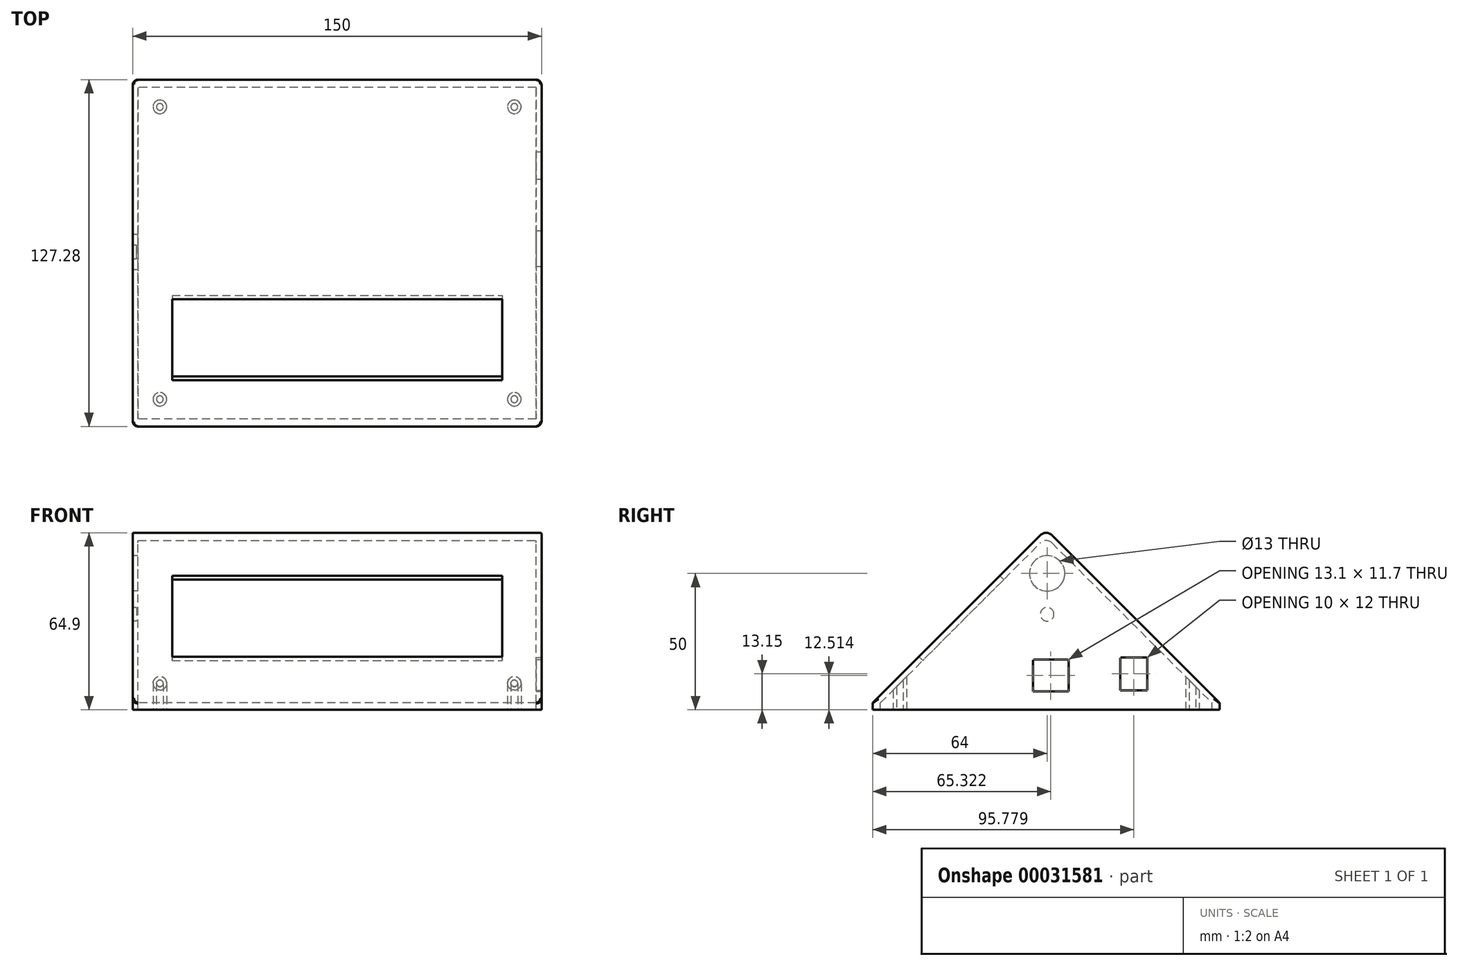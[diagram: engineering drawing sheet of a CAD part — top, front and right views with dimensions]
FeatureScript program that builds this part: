
annotation { "Feature Type Name" : "Feature", "Feature Type Description" : "" }
export const myFeature = defineFeature(function(context is Context, id is Id, definition is map)
    precondition{}
    {
        {
            var Q0;
            Q0=qCreatedBy(makeId("Right.planeOp"),FACE);
            var sketch = newSketch(context, id + "F0", { "sketchPlane" : qUnion([Q0])});
            skLineSegment(sketch, "E0", {"start": v(0, 0) * mm, "end": v(63.64, 63.64) * mm});
            skLineSegment(sketch, "E1", {"start": v(63.64, 63.64) * mm, "end": v(127.28, 0) * mm});
            skLineSegment(sketch, "E2", {"start": v(127.28, 0) * mm, "end": v(0, 0) * mm});
            skSolve(sketch);
        }
        {
            var Q0;
            Q0=qSketchRegion(id+"F0",true);
            extrude(context, id + "F1", {"entities" : qUnion([Q0]), "depth" : 150 * mm});
        }
        {
            var Q0;
            Q0=makeQuery(id+"F1.opExtrude","SWEPT_FACE",FACE,{"disambiguationData":[OSD([sQuery(id+"F0.wireOp",EDGE,"E2")])]});
            shell(context, id + "F2", {"entities" : qUnion([Q0]), "thickness" : 2 * mm});
        }
        {
            var Q0;
            Q0=makeQuery(id+"F1.opExtrude","SWEPT_FACE",FACE,{"disambiguationData":[OSD([sQuery(id+"F0.wireOp",EDGE,"E0")])]});
            cPlane(context, id + "F3", {"entities" : qUnion([Q0]), "cplaneType" : CPlaneType.OFFSET, "offset" : 0 * mm, "width" : 150 * mm, "height" : 150 * mm});
        }
        {
            var Q0;
            Q0=qCreatedBy(id+"F3.planeOp",FACE);
            var sketch = newSketch(context, id + "F4", { "sketchPlane" : qUnion([Q0])});
            skLineSegment(sketch, "E3.bottom", {"start": v(14.5, 66) * mm, "end": v(135.5, 66) * mm});
            skLineSegment(sketch, "E3.top", {"start": v(14.5, 24) * mm, "end": v(135.5, 24) * mm});
            skLineSegment(sketch, "E3.left", {"start": v(14.5, 66) * mm, "end": v(14.5, 24) * mm});
            skLineSegment(sketch, "E3.right", {"start": v(135.5, 66) * mm, "end": v(135.5, 24) * mm});
            skLineSegment(sketch, "E4", {"start": v(14.5, 45) * mm, "end": v(90.75, 45) * mm, "construction": true});
            skSolve(sketch);
        }
        {
            var Q0;
            Q0=qSketchRegion(id+"F4",true);
            extrude(context, id + "F5", {"entities" : qUnion([Q0]), "operationType" : NewBodyOperationType.REMOVE, "oppositeDirection" : true, "depth" : 3 * mm});
        }
        {
            var Q0;
            Q0=makeQuery(id+"F1.opExtrude","SWEPT_EDGE",EDGE,{"disambiguationData":[OSD([sQuery(id+"F0.wireOp",EDGE,"E0"),sQuery(id+"F0.wireOp",EDGE,"E1")])]});
            fillet(context, id + "F6", {"entities" : qUnion([Q0]), "radius" : 3 * mm, "tangentPropagation" : true, "allowEdgeOverflow" : false});
        }
        {
            var Q0;
            Q0=makeQuery(id+"F1.opExtrude","CAP_FACE",FACE,{"disambiguationData":[OSD([sQuery(id+"F0.wireOp",EDGE,"E0"),sQuery(id+"F0.wireOp",EDGE,"E1"),sQuery(id+"F0.wireOp",EDGE,"E2")])],"isStart":false});
            var sketch = newSketch(context, id + "F7", { "sketchPlane" : qUnion([Q0])});
            skCircle(sketch, "E5", {"center": v(70, 8) * mm, "radius": 6 * mm, "construction": true});
            skLineSegment(sketch, "E6.bottom", {"start": v(90.78, 4.65) * mm, "end": v(100.78, 4.65) * mm});
            skLineSegment(sketch, "E6.top", {"start": v(90.78, 16.65) * mm, "end": v(100.78, 16.65) * mm});
            skLineSegment(sketch, "E6.left", {"start": v(90.78, 4.65) * mm, "end": v(90.78, 16.65) * mm});
            skLineSegment(sketch, "E6.right", {"start": v(100.78, 4.65) * mm, "end": v(100.78, 16.65) * mm});
            skLineSegment(sketch, "E7.bottom", {"start": v(59.27, 15.36) * mm, "end": v(71.37, 15.36) * mm, "construction": true});
            skLineSegment(sketch, "E7.top", {"start": v(59.27, 4.66) * mm, "end": v(71.37, 4.66) * mm, "construction": true});
            skLineSegment(sketch, "E7.left", {"start": v(59.27, 15.36) * mm, "end": v(59.27, 4.66) * mm, "construction": true});
            skLineSegment(sketch, "E7.right", {"start": v(71.37, 15.36) * mm, "end": v(71.37, 4.66) * mm, "construction": true});
            skLineSegment(sketch, "E8", {"start": v(71.87, 15.86) * mm, "end": v(58.77, 15.86) * mm});
            skLineSegment(sketch, "E9", {"start": v(58.77, 15.86) * mm, "end": v(58.77, 4.16) * mm});
            skLineSegment(sketch, "E10", {"start": v(58.77, 4.16) * mm, "end": v(71.87, 4.16) * mm});
            skLineSegment(sketch, "E11", {"start": v(71.87, 15.86) * mm, "end": v(71.87, 4.16) * mm});
            skSolve(sketch);
        }
        {
            var Q0;
            Q0=makeQuery(id+"F1.opExtrude","SWEPT_FACE",FACE,{"disambiguationData":[OSD([sQuery(id+"F0.wireOp",EDGE,"E2")])]});
            var sketch = newSketch(context, id + "F8", { "sketchPlane" : qUnion([Q0])});
            skCircle(sketch, "E12", {"center": v(10, -10) * mm, "radius": 1.5 * mm});
            skCircle(sketch, "E13", {"center": v(10, -10) * mm, "radius": 2.5 * mm});
            skSolve(sketch);
        }
        {
            var Q0;
            Q0=qSketchRegion(id+"F8",true);
            var Q1;
            Q1=makeQuery(id+"F1.opExtrude","SWEPT_FACE",FACE,{"disambiguationData":[OSD([sQuery(id+"F0.wireOp",EDGE,"E0")])]});
            extrude(context, id + "F9", {"entities" : qUnion([Q0]), "operationType" : NewBodyOperationType.ADD, "endBound" : BoundingType.UP_TO_SURFACE, "oppositeDirection" : true, "endBoundEntityFace" : qUnion([Q1]), "depth" : 25 * mm});
        }
        {
            var Q0;
            Q0=makeQuery(id+"F1.opExtrude","SWEPT_FACE",FACE,{"disambiguationData":[OSD([sQuery(id+"F0.wireOp",EDGE,"E2")])]});
            var sketch = newSketch(context, id + "F10", { "sketchPlane" : qUnion([Q0])});
            skCircle(sketch, "E14", {"center": v(10, -117.28) * mm, "radius": 2.5 * mm, "construction": true});
            skCircle(sketch, "E15", {"center": v(10, -117.28) * mm, "radius": 1.5 * mm, "construction": true});
            skCircle(sketch, "E16", {"center": v(140, -117.28) * mm, "radius": 1.5 * mm, "construction": true});
            skCircle(sketch, "E17", {"center": v(140, -117.28) * mm, "radius": 2.5 * mm, "construction": true});
            skCircle(sketch, "E18", {"center": v(10, -10) * mm, "radius": 1.25 * mm});
            skCircle(sketch, "E19", {"center": v(10, -10) * mm, "radius": 2.5 * mm});
            skCircle(sketch, "E20", {"center": v(140, -10) * mm, "radius": 1.25 * mm});
            skCircle(sketch, "E21", {"center": v(140, -10) * mm, "radius": 2.5 * mm});
            skSolve(sketch);
        }
        {
            var Q0;
            Q0=qSketchRegion(id+"F10",true);
            var Q1;
            {var subQ1=sQuery(id+"F0.wireOp",EDGE,"E2");var subQ2=sQuery(id+"F0.wireOp",EDGE,"E0");Q1=makeQuery(id+"F9.boolean.opBoolean","SPLIT",FACE,{"disambiguationData":[TD([makeQuery(id+"F1.opExtrude","SWEPT_FACE",FACE,{"disambiguationData":[OSD([subQ1])]})])],"derivedFrom":makeQuery(id+"F2.opShell","OFFSET_FACE",FACE,{"disambiguationData":[OSD([subQ2])]})});}
            extrude(context, id + "F11", {"entities" : qUnion([Q0]), "operationType" : NewBodyOperationType.ADD, "endBound" : BoundingType.UP_TO_SURFACE, "oppositeDirection" : true, "endBoundEntityFace" : qUnion([Q1]), "depth" : 25 * mm});
        }
        {
            var Q0;
            Q0=makeQuery(id+"F1.opExtrude","SWEPT_FACE",FACE,{"disambiguationData":[OSD([sQuery(id+"F0.wireOp",EDGE,"E2")])]});
            var sketch = newSketch(context, id + "F12", { "sketchPlane" : qUnion([Q0])});
            skLineSegment(sketch, "E22.bottom", {"start": v(0, 0) * mm, "end": v(150, 0) * mm});
            skLineSegment(sketch, "E22.top", {"start": v(0, -127.28) * mm, "end": v(150, -127.28) * mm});
            skLineSegment(sketch, "E22.left", {"start": v(0, 0) * mm, "end": v(0, -127.28) * mm});
            skLineSegment(sketch, "E22.right", {"start": v(150, 0) * mm, "end": v(150, -127.28) * mm});
            skLineSegment(sketch, "E23.bottom", {"start": v(148, -124.45) * mm, "end": v(2, -124.45) * mm});
            skLineSegment(sketch, "E23.top", {"start": v(148, -2.83) * mm, "end": v(2, -2.83) * mm});
            skLineSegment(sketch, "E23.left", {"start": v(148, -124.45) * mm, "end": v(148, -2.83) * mm});
            skLineSegment(sketch, "E23.right", {"start": v(2, -124.45) * mm, "end": v(2, -2.83) * mm});
            skSolve(sketch);
        }
        {
            var Q0;
            Q0=qSketchRegion(id+"F12",true);
            extrude(context, id + "F13", {"entities" : qUnion([Q0]), "operationType" : NewBodyOperationType.ADD, "depth" : 2.5 * mm});
        }
        {
            var Q0;
            Q0=qCreatedBy(makeId("Top.planeOp"),FACE);
            var sketch = newSketch(context, id + "F14", { "sketchPlane" : qUnion([Q0])});
            skCircle(sketch, "E24", {"center": v(10, 117.28) * mm, "radius": 1.25 * mm});
            skCircle(sketch, "E25.0", {"center": v(10, 10) * mm, "radius": 2.5 * mm, "construction": true});
            skCircle(sketch, "E26", {"center": v(10, 117.28) * mm, "radius": 2.5 * mm});
            skCircle(sketch, "E27", {"center": v(140, 117.28) * mm, "radius": 1.25 * mm});
            skCircle(sketch, "E28", {"center": v(140, 117.28) * mm, "radius": 2.5 * mm});
            skCircle(sketch, "E29.0", {"center": v(140, 10) * mm, "radius": 1.25 * mm});
            skSolve(sketch);
        }
        {
            var Q0;
            Q0=makeQuery(id+"F14.imprint","IMPRINT",FACE,{"disambiguationData":[TD([[makeQuery(id+"F14.imprint","IMPRINT",EDGE,{"derivedFrom":sQuery(id+"F14.wireOp",EDGE,"E27")}),-1.0]])]});
            var Q1;
            Q1=makeQuery(id+"F14.imprint","IMPRINT",FACE,{"disambiguationData":[TD([[makeQuery(id+"F14.imprint","IMPRINT",EDGE,{"derivedFrom":sQuery(id+"F14.wireOp",EDGE,"E24")}),-1.0]])]});
            var Q2;
            Q2=makeQuery(id+"F2.opShell","OFFSET_FACE",FACE,{"disambiguationData":[OSD([sQuery(id+"F0.wireOp",EDGE,"E1")])]});
            extrude(context, id + "F15", {"entities" : qUnion([Q0, Q1]), "operationType" : NewBodyOperationType.ADD, "endBound" : BoundingType.UP_TO_SURFACE, "endBoundEntityFace" : qUnion([Q2]), "depth" : 25 * mm});
        }
        {
            var Q0;
            Q0=makeQuery(id+"F13.opExtrude","SWEPT_EDGE",EDGE,{"disambiguationData":[OSD([sQuery(id+"F12.wireOp",EDGE,"E22.top"),sQuery(id+"F12.wireOp",EDGE,"E22.right")])]});
            var Q1;
            Q1=makeQuery(id+"F13.opExtrude","SWEPT_EDGE",EDGE,{"disambiguationData":[OSD([sQuery(id+"F12.wireOp",EDGE,"E22.bottom"),sQuery(id+"F12.wireOp",EDGE,"E22.right")])]});
            var Q2;
            Q2=makeQuery(id+"F13.opExtrude","SWEPT_EDGE",EDGE,{"disambiguationData":[OSD([sQuery(id+"F12.wireOp",EDGE,"E22.bottom"),sQuery(id+"F12.wireOp",EDGE,"E22.left")])]});
            var Q3;
            Q3=makeQuery(id+"F13.opExtrude","SWEPT_EDGE",EDGE,{"disambiguationData":[OSD([sQuery(id+"F12.wireOp",EDGE,"E22.top"),sQuery(id+"F12.wireOp",EDGE,"E22.left")])]});
            fillet(context, id + "F16", {"entities" : qUnion([Q0, Q1, Q2, Q3]), "radius" : 2 * mm, "tangentPropagation" : true, "allowEdgeOverflow" : false});
        }
        {
            var Q0;
            Q0=makeQuery(id+"F1.opExtrude","CAP_EDGE",EDGE,{"disambiguationData":[OSD([sQuery(id+"F0.wireOp",EDGE,"E0")])],"isStart":true});
            fillet(context, id + "F17", {"entities" : qUnion([Q0]), "radius" : 0.5 * mm, "tangentPropagation" : true, "allowEdgeOverflow" : false});
        }
        {
            var Q0;
            Q0=qSketchRegion(id+"F7",true);
            extrude(context, id + "F18", {"entities" : qUnion([Q0]), "operationType" : NewBodyOperationType.REMOVE, "oppositeDirection" : true, "depth" : 3 * mm});
        }
        {
            var Q0;
            Q0=makeQuery(id+"F18.boolean.opBoolean","COPY",EDGE,{"derivedFrom":makeQuery(id+"F18.opExtrude","SWEPT_EDGE",EDGE,{"disambiguationData":[OSD([sQuery(id+"F7.wireOp",EDGE,"E6.top"),sQuery(id+"F7.wireOp",EDGE,"E6.left")])]})});
            var Q1;
            Q1=makeQuery(id+"F18.boolean.opBoolean","COPY",EDGE,{"derivedFrom":makeQuery(id+"F18.opExtrude","SWEPT_EDGE",EDGE,{"disambiguationData":[OSD([sQuery(id+"F7.wireOp",EDGE,"E6.top"),sQuery(id+"F7.wireOp",EDGE,"E6.right")])]})});
            fillet(context, id + "F19", {"entities" : qUnion([Q0, Q1]), "radius" : 0.5 * mm, "tangentPropagation" : true, "allowEdgeOverflow" : false});
        }
        {
            var Q0;
            Q0=makeQuery(id+"F18.boolean.opBoolean","COPY",EDGE,{"derivedFrom":makeQuery(id+"F18.opExtrude","SWEPT_EDGE",EDGE,{"disambiguationData":[OSD([sQuery(id+"F7.wireOp",EDGE,"E8"),sQuery(id+"F7.wireOp",EDGE,"E11")])]})});
            var Q1;
            Q1=makeQuery(id+"F18.boolean.opBoolean","COPY",EDGE,{"derivedFrom":makeQuery(id+"F18.opExtrude","SWEPT_EDGE",EDGE,{"disambiguationData":[OSD([sQuery(id+"F7.wireOp",EDGE,"E8"),sQuery(id+"F7.wireOp",EDGE,"E9")])]})});
            fillet(context, id + "F20", {"entities" : qUnion([Q0, Q1]), "radius" : .5 * mm, "tangentPropagation" : true, "allowEdgeOverflow" : false});
        }
        {
            var Q0;
            Q0=makeQuery(id+"F13.boolean.opBoolean","MERGE",FACE,{"derivedFrom":[makeQuery(id+"F1.opExtrude","CAP_FACE",FACE,{"disambiguationData":[OSD([sQuery(id+"F0.wireOp",EDGE,"E0"),sQuery(id+"F0.wireOp",EDGE,"E1"),sQuery(id+"F0.wireOp",EDGE,"E2")])],"isStart":true}),makeQuery(id+"F13.opExtrude","SWEPT_FACE",FACE,{"disambiguationData":[OSD([sQuery(id+"F12.wireOp",EDGE,"E22.left")])]})]});
            var sketch = newSketch(context, id + "F21", { "sketchPlane" : qUnion([Q0])});
            skCircle(sketch, "E30", {"center": v(-64, 47.5) * mm, "radius": 6.5 * mm});
            skSolve(sketch);
        }
        {
            var Q0;
            Q0=makeQuery(id+"F21.imprint","IMPRINT",FACE,{"disambiguationData":[TD([[makeQuery(id+"F21.imprint","IMPRINT",EDGE,{"derivedFrom":sQuery(id+"F21.wireOp",EDGE,"E30")}),1.0]])]});
            var Q1;
            Q1=sQuery(id+"F21.wireOp",EDGE,"E30");
            extrude(context, id + "F22", {"entities" : qUnion([Q0]), "operationType" : NewBodyOperationType.REMOVE, "surfaceEntities" : qUnion([Q1]), "oppositeDirection" : true, "depth" : 2.5 * mm});
        }
        {
            var Q0;
            Q0=makeQuery(id+"F11.opExtrude","CAP_FACE",FACE,{"disambiguationData":[OSD([sQuery(id+"F10.wireOp",EDGE,"E20"),sQuery(id+"F10.wireOp",EDGE,"E21")])],"isStart":true});
            var sketch = newSketch(context, id + "F23", { "sketchPlane" : qUnion([Q0])});
            skCircle(sketch, "E31", {"center": v(140, -10) * mm, "radius": 1.25 * mm});
            skCircle(sketch, "E32.0", {"center": v(10, -10) * mm, "radius": 1.25 * mm});
            skCircle(sketch, "E33.0", {"center": v(10, -10) * mm, "radius": 2.5 * mm});
            skCircle(sketch, "E34.0", {"center": v(140, -10) * mm, "radius": 2.5 * mm});
            skCircle(sketch, "E35.0", {"center": v(10, -117.28) * mm, "radius": 1.25 * mm});
            skCircle(sketch, "E36.0", {"center": v(10, -117.28) * mm, "radius": 2.5 * mm});
            skCircle(sketch, "E37.0", {"center": v(140, -117.28) * mm, "radius": 1.25 * mm});
            skCircle(sketch, "E38.0", {"center": v(140, -117.28) * mm, "radius": 2.5 * mm});
            skSolve(sketch);
        }
        {
            var Q0;
            Q0 = qSketchRegion(id + "F23", true);
            extrude(context, id + "F24", {"entities" : qUnion([Q0]), "operationType" : NewBodyOperationType.ADD, "depth" : 2.5 * mm});
        }
        {
            var Q0;
            Q0=makeQuery(id+"F13.boolean.opBoolean","MERGE",FACE,{"derivedFrom":[makeQuery(id+"F1.opExtrude","CAP_FACE",FACE,{"disambiguationData":[OSD([sQuery(id+"F0.wireOp",EDGE,"E0"),sQuery(id+"F0.wireOp",EDGE,"E1"),sQuery(id+"F0.wireOp",EDGE,"E2")])],"isStart":true}),makeQuery(id+"F13.opExtrude","SWEPT_FACE",FACE,{"disambiguationData":[OSD([sQuery(id+"F12.wireOp",EDGE,"E22.left")])]})]});
            var sketch = newSketch(context, id + "F25", { "sketchPlane" : qUnion([Q0])});
            skCircle(sketch, "E39", {"center": v(-64, 32.5) * mm, "radius": 2.5 * mm});
            skCircle(sketch, "E40.0", {"center": v(-64, 47.5) * mm, "radius": 6.5 * mm, "construction": true});
            skCircle(sketch, "E41", {"center": v(-64, 47.5) * mm, "radius": 7 * mm, "construction": true});
            skSolve(sketch);
        }
        {
            var Q0;
            Q0=makeQuery(id+"F25.imprint","IMPRINT",FACE,{"disambiguationData":[TD([[makeQuery(id+"F25.imprint","IMPRINT",EDGE,{"derivedFrom":sQuery(id+"F25.wireOp",EDGE,"E39")}),1.0]])]});
            var Q1;
            Q1=sQuery(id+"F25.wireOp",EDGE,"E41");
            var Q2;
            Q2=sQuery(id+"F25.wireOp",EDGE,"E40.0");
            extrude(context, id + "F26", {"entities" : qUnion([Q0]), "operationType" : NewBodyOperationType.REMOVE, "surfaceEntities" : qUnion([Q1, Q2]), "oppositeDirection" : true, "depth" : 1.5 * mm});
        }
        {
            var Q0;
            Q0=makeQuery(id+"F2.opShell","OFFSET_EDGE",EDGE,{"disambiguationData":[OSD([sQuery(id+"F0.wireOp",EDGE,"E0"),sQuery(id+"F0.wireOp",EDGE,"E1")])]});
            fillet(context, id + "F27", {"entities" : qUnion([Q0]), "radius" : 3 * mm, "tangentPropagation" : true, "allowEdgeOverflow" : false});
        }
    });
